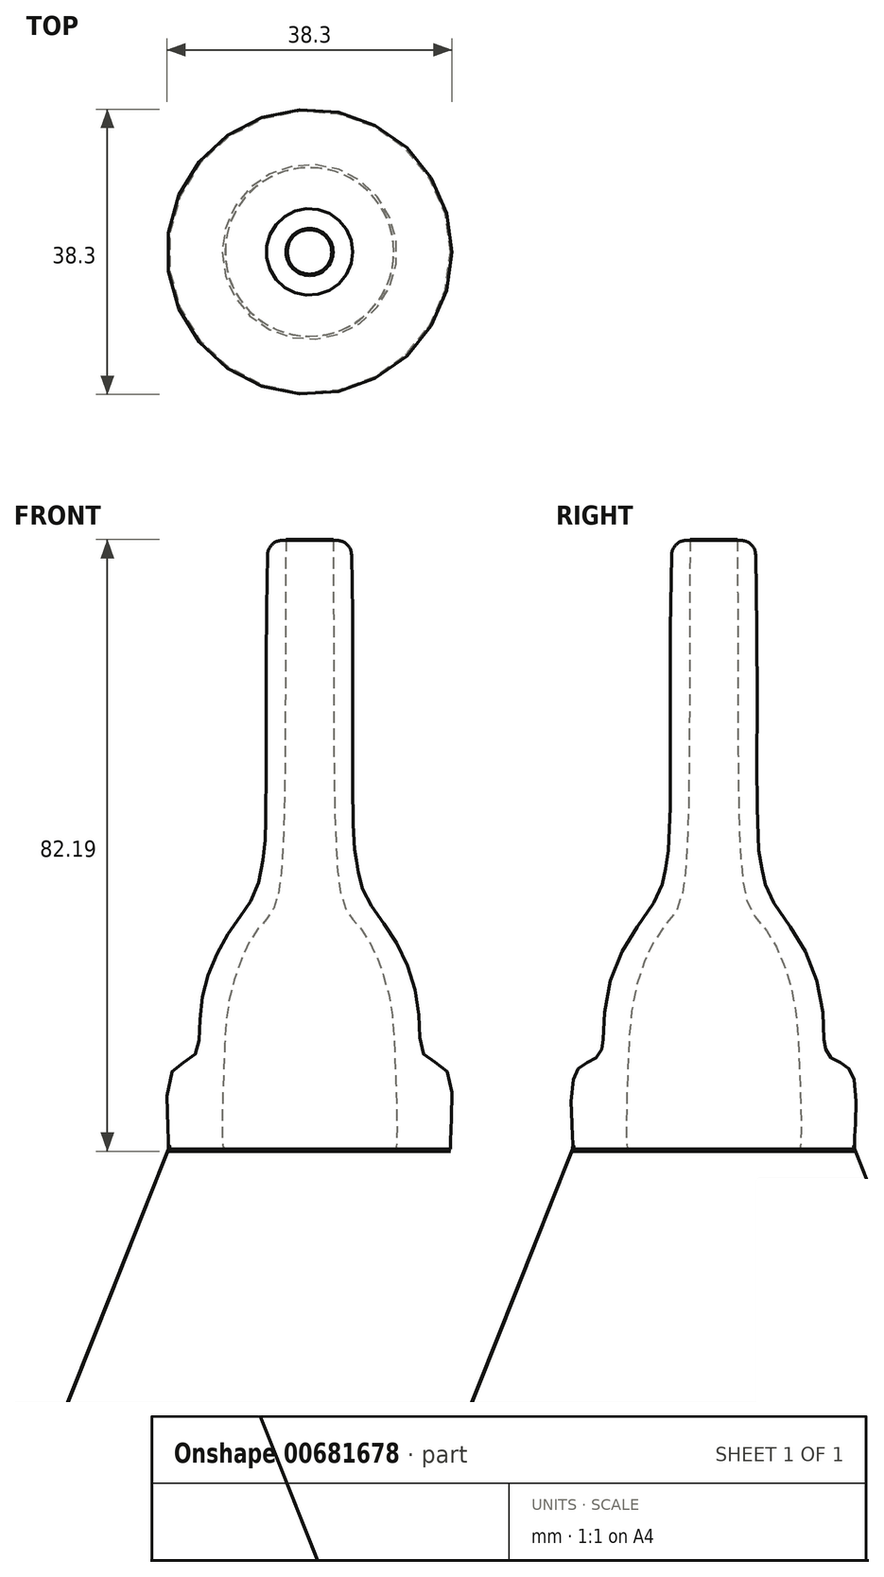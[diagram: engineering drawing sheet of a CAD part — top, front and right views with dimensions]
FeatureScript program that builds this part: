
annotation { "Feature Type Name" : "Feature", "Feature Type Description" : "" }
export const myFeature = defineFeature(function(context is Context, id is Id, definition is map)
    precondition{}
    {
        {
            var Q0;
            Q0=qCreatedBy(makeId("Right.planeOp"),FACE);
            var sketch = newSketch(context, id + "F0", { "sketchPlane" : qUnion([Q0])});
            skLineSegment(sketch, "E0", {"start": v(0, 43.1) * mm, "end": v(0, -38.9) * mm});
            skSolve(sketch);
        }
        {
            var Q0;
            Q0=qCreatedBy(makeId("Right.planeOp"),FACE);
            var sketch = newSketch(context, id + "F1", { "sketchPlane" : qUnion([Q0])});
            skFitSpline(sketch, "E1", {"points": [v(-3.18, 43.46) * mm, v(-3.54, 2.45) * mm, v(-4.99, -6.44) * mm, v(-7.17, -9.16) * mm, v(-10.43, -16.78) * mm, v(-11.52, -27.49) * mm, v(-11.52, -38.56) * mm, v(-11.34, -38.56) * mm], "startDerivative": vector(-1.45, -165.92) * mm, "endDerivative": vector(10.1, 4.85) * mm});
            skSolve(sketch);
        }
        {
            var Q0;
            Q0=qCreatedBy(makeId("Right.planeOp"),FACE);
            var sketch = newSketch(context, id + "F2", { "sketchPlane" : qUnion([Q0])});
            skFitSpline(sketch, "E2", {"points": [v(-5.59, 43.36) * mm, v(-6, 2.24) * mm, v(-6.36, 0) * mm, v(-7.26, -3.85) * mm, v(-11.2, -9.95) * mm, v(-14.6, -19.45) * mm, v(-15.5, -25.9) * mm, v(-18.37, -27.87) * mm, v(-18.96, -36.66) * mm, v(-18.96, -38.45) * mm], "startDerivative": vector(-5.44, -171.45) * mm, "endDerivative": vector(-0.7, 15.25) * mm});
            skLineSegment(sketch, "E3", {"start": v(-11.31, -38.47) * mm, "end": v(-18.94, -38.73) * mm});
            skLineSegment(sketch, "E4", {"start": v(-2.99, 43.36) * mm, "end": v(-5.59, 43.36) * mm});
            skSolve(sketch);
        }
        {
            var Q0;
            Q0 = qSketchRegion(id + "F2", true);
            var Q1;
            Q1=sQuery(id+"F2.wireOp",EDGE,"E2");
            var Q2;
            Q2=sQuery(id+"F2.wireOp",EDGE,"E3");
            var Q3;
            Q3=sQuery(id+"F2.wireOp",EDGE,"E4");
            var Q4;
            Q4=sQuery(id+"F0.wireOp",EDGE,"E0");
            revolve(context, id + "F3", {"bodyType" : ToolBodyType.SURFACE, "operationType" : NewBodyOperationType.REMOVE, "surfaceOperationType" : NewSurfaceOperationType.NEW, "entities" : qUnion([Q0]), "surfaceEntities" : qUnion([Q1, Q2, Q3]), "axis" : qUnion([Q4]), "revolveType" : RevolveType.FULL, "oppositeDirection" : true});
        }
        {
            var Q0;
            Q0 = qConstructionFilter(qBodyType(qCreatedBy(id + "F1" ,EDGE), BodyType.WIRE), ConstructionObject.NO);
            var Q1;
            Q1=sQuery(id+"F0.wireOp",EDGE,"E0");
            revolve(context, id + "F4", {"bodyType" : ToolBodyType.SURFACE, "surfaceOperationType" : NewSurfaceOperationType.NEW, "surfaceEntities" : qUnion([Q0]), "axis" : qUnion([Q1]), "revolveType" : RevolveType.FULL});
        }
        {
            var Q0;
            Q0=sQuery(id+"F2.wireOp",EDGE,"E3");
            var Q1;
            Q1=sQuery(id+"F0.wireOp",EDGE,"E0");
            revolve(context, id + "F5", {"bodyType" : ToolBodyType.SURFACE, "surfaceOperationType" : NewSurfaceOperationType.NEW, "surfaceEntities" : qUnion([Q0]), "axis" : qUnion([Q1]), "revolveType" : RevolveType.FULL});
        }
        {
            var Q0;
            Q0=makeQuery(id+"F3.opRevolve","SWEPT_FACE",FACE,{"disambiguationData":[OSD([sQuery(id+"F2.wireOp",EDGE,"E2")])]});
            var Q1;
            Q1=makeQuery(id+"F3.opRevolve","SWEPT_FACE",FACE,{"disambiguationData":[OSD([sQuery(id+"F2.wireOp",EDGE,"E4")])]});
            fillet(context, id + "F6", {"entities" : qUnion([Q0, Q1]), "radius" : 2 * mm, "allowEdgeOverflow" : false});
        }
    });
